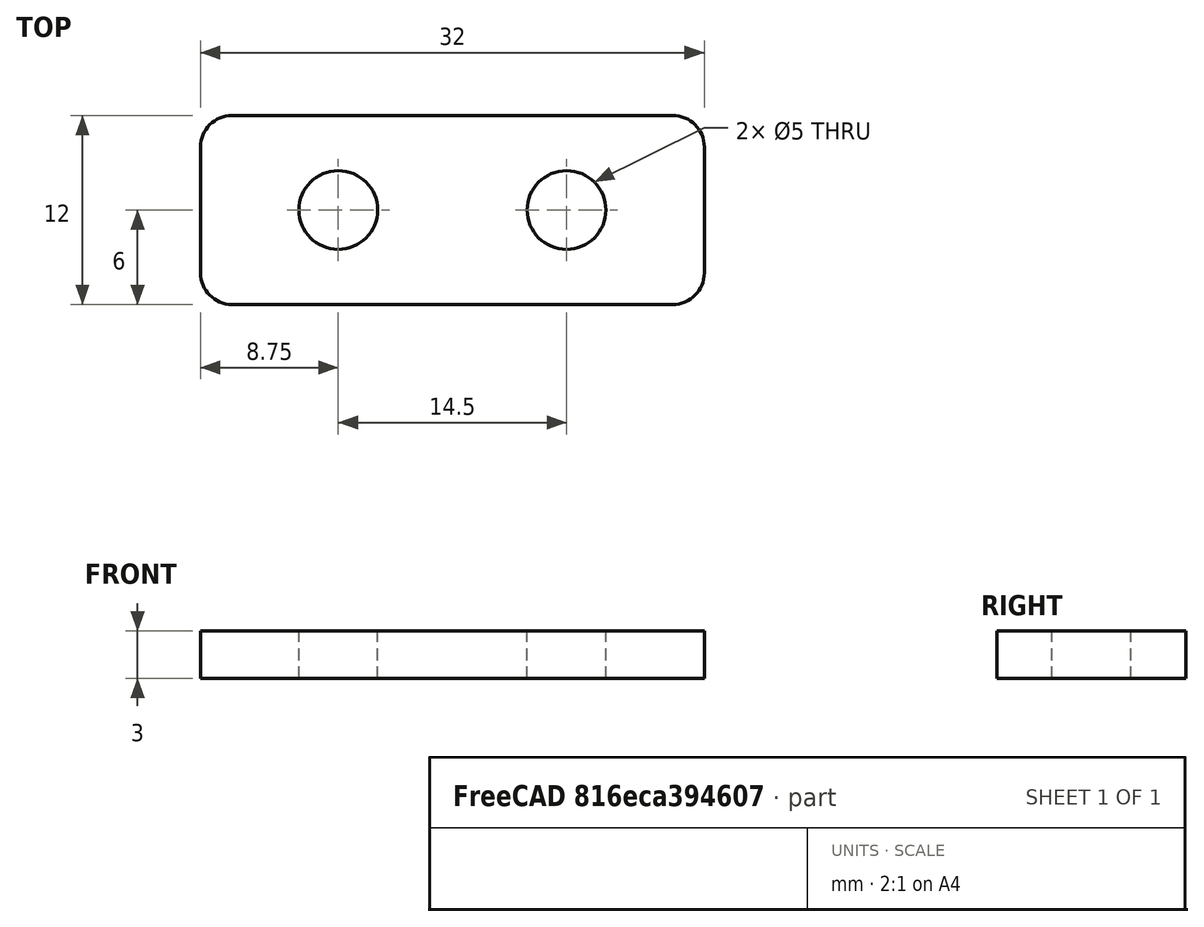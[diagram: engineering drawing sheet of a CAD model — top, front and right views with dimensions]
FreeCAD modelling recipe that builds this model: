
FCSTD DOCUMENT  (FreeCAD 0.17R13541 (Git))
Label: SujetaCable14.5mm
License: All rights reserved
LicenseURL: http://en.wikipedia.org/wiki/All_rights_reserved
objects: Part::Cylinder×2, Part::Box×1, Part::MultiFuse×1, Part::Cut×1, Part::Fillet×1, Part::Feature×1
note: 7 computed .brp shape members not serialized (recipe doc carries the construction recipe); baked Part::Feature solids carry a one-line shape summary decoded from their .brp

FEATURE [Part::Box] Box  label="Cubo"
  AttacherType = Attacher::AttachEngine3D
  Height = 3
  Length = 32
  Width = 12
FEATURE [Part::Cylinder] Cylinder  label="Cilindro"
  Angle = 360
  AttacherType = Attacher::AttachEngine3D
  Height = 10
  Placement = pos=(8.75,6,-7) rot=(0,0,1;0rad)
  Radius = 2.5
FEATURE [Part::Cylinder] Cylinder001  label="Cilindro001"
  Angle = 360
  AttacherType = Attacher::AttachEngine3D
  Height = 10
  Placement = pos=(23.25,6,-7) rot=(0,0,1;0rad)
  Radius = 2.5
FEATURE [Part::MultiFuse] Fusion
  Refine = true
  Shapes = -> [Cylinder001,Cylinder]
FEATURE [Part::Cut] Cut
  Base = -> Box
  Refine = true
  Tool = -> Fusion
FEATURE [Part::Fillet] Fillet  label="SujetaCable14.5mm-Terminado"
  Base = -> Cut
  Edges = 4 edges r=2: [Edge1,Edge3,Edge6,Edge13]
FEATURE [Part::Feature] Fillet001  label="SujetaCable14.5mm-CopiaSimple"
  shape: bbox 32 x 12 x 3 mm, 12 faces (baked)
